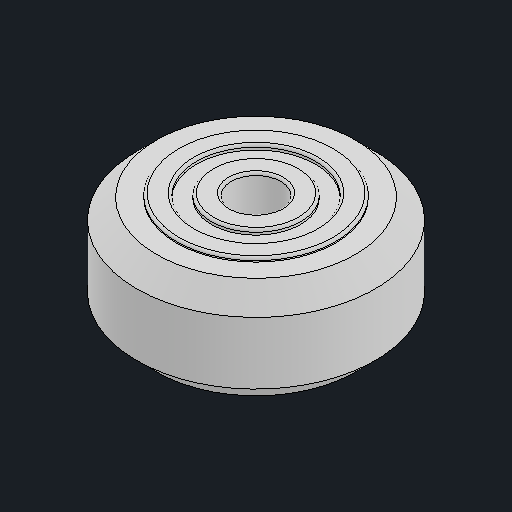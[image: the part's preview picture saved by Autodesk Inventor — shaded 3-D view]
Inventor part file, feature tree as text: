
AUTODESK INVENTOR PART (.ipt)
format: ipt  version: 2024.2 (Build 282272000, 272)  size: 163,328 bytes
history: native  units: mm
features: other x2, chamfer x1, fillet x1
ambient origin geometry x8: Origin, YZ Plane, XZ Plane, XY Plane, X Axis, Y Axis, Z Axis, Center Point
bodies: Body1 (feature_tree), Body2 (feature_tree)
feature tree (4):
  other  "솔리드1"
  other  "솔리드2"
  chamfer  "Chamfer1"  [1 undecoded]
  fillet  "Fillet1"  [1 undecoded]
note: 2 required parameter values undecoded (feature->parameter linkage not recoverable at this tier; creation-order binding heuristic only, values carry confidence <= 0.55)
